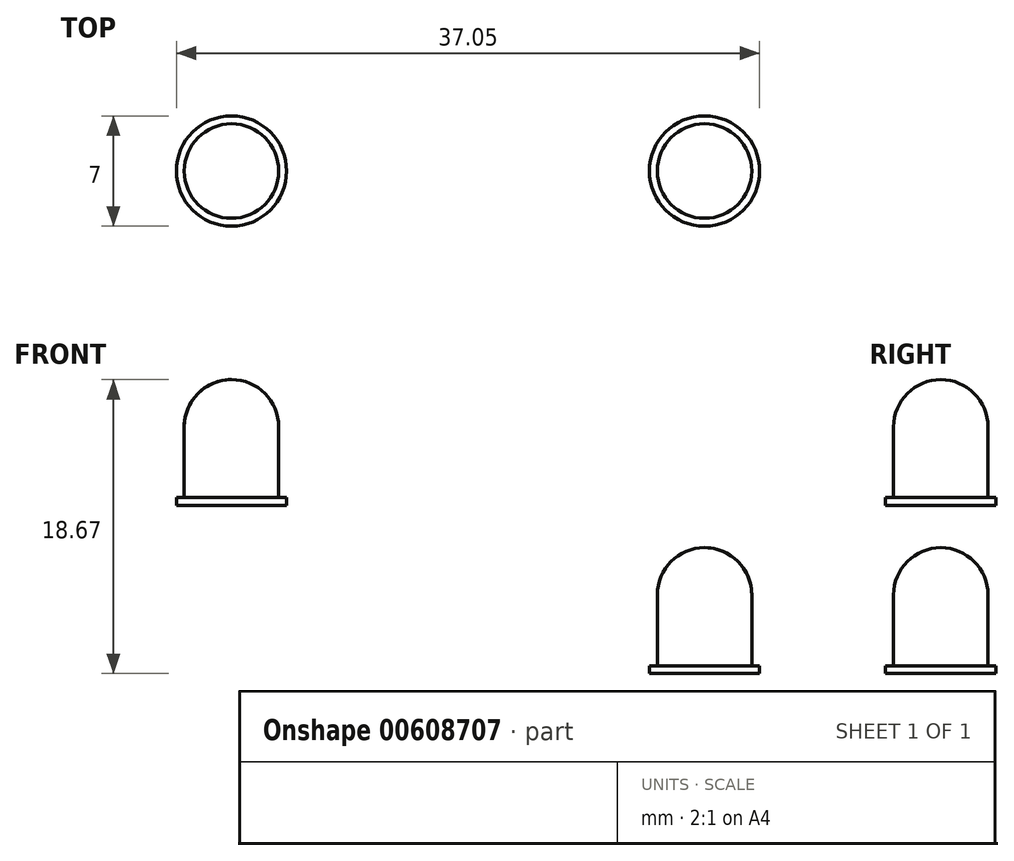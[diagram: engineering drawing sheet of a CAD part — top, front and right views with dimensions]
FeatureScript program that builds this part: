
annotation { "Feature Type Name" : "Feature", "Feature Type Description" : "" }
export const myFeature = defineFeature(function(context is Context, id is Id, definition is map)
    precondition{}
    {
        {
            var Q0;
            Q0=qCreatedBy(makeId("Front.planeOp"),FACE);
            var sketch = newSketch(context, id + "F0", { "sketchPlane" : qUnion([Q0])});
            skLineSegment(sketch, "E0", {"start": v(-49.36, 24) * mm, "end": v(-52.86, 24) * mm});
            skLineSegment(sketch, "E1", {"start": v(-52.86, 24) * mm, "end": v(-52.86, 24.5) * mm});
            skLineSegment(sketch, "E2", {"start": v(-52.86, 24.5) * mm, "end": v(-52.36, 24.5) * mm});
            skLineSegment(sketch, "E3", {"start": v(-52.36, 24.5) * mm, "end": v(-52.36, 29) * mm});
            skArc(sketch, "E4", {"start": v(-52.36, 29) * mm, "mid": v(-51.48, 31.13) * mm, "end": v(-49.36, 32) * mm});
            skLineSegment(sketch, "E5", {"start": v(-49.36, 32) * mm, "end": v(-49.36, 24) * mm});
            skSolve(sketch);
        }
        {
            var Q0;
            Q0 = qSketchRegion(id + "F0", true);
            var Q1;
            Q1=sQuery(id+"F0.wireOp",EDGE,"E5");
            revolve(context, id + "F1", {"entities" : qUnion([Q0]), "axis" : qUnion([Q1]), "revolveType" : RevolveType.FULL});
        }
        {
            var Q0;
            Q0=qCreatedBy(makeId("Front.planeOp"),FACE);
            var sketch = newSketch(context, id + "F2", { "sketchPlane" : qUnion([Q0])});
            skLineSegment(sketch, "E6", {"start": v(-19.31, 13.33) * mm, "end": v(-22.81, 13.33) * mm});
            skLineSegment(sketch, "E7", {"start": v(-22.81, 13.33) * mm, "end": v(-22.81, 13.83) * mm});
            skLineSegment(sketch, "E8", {"start": v(-22.81, 13.83) * mm, "end": v(-22.31, 13.83) * mm});
            skLineSegment(sketch, "E9", {"start": v(-22.31, 13.83) * mm, "end": v(-22.31, 18.33) * mm});
            skArc(sketch, "E10", {"start": v(-22.31, 18.33) * mm, "mid": v(-21.44, 20.45) * mm, "end": v(-19.31, 21.33) * mm});
            skLineSegment(sketch, "E11", {"start": v(-19.31, 21.33) * mm, "end": v(-19.31, 13.33) * mm});
            skSolve(sketch);
        }
        {
            var Q0;
            Q0=makeQuery(id+"F2.imprint","IMPRINT",FACE,{"disambiguationData":[TD([[makeQuery(id+"F2.imprint","IMPRINT",EDGE,{"derivedFrom":sQuery(id+"F2.wireOp",EDGE,"E6")}),-1.0]])]});
            var Q1;
            Q1 = qConstructionFilter(qBodyType(qCreatedBy(id + "F2" ,EDGE), BodyType.WIRE), ConstructionObject.NO);
            var Q2;
            Q2=sQuery(id+"F2.wireOp",EDGE,"E11");
            revolve(context, id + "F3", {"entities" : qUnion([Q0]), "surfaceEntities" : qUnion([Q1]), "axis" : qUnion([Q2]), "revolveType" : RevolveType.FULL});
        }
    });
